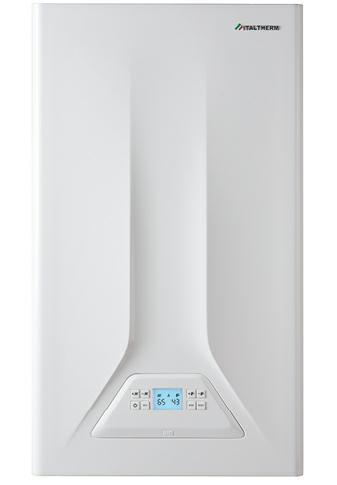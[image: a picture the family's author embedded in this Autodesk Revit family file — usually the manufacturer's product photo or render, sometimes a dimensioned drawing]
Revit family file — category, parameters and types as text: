
# Revit family: City Top H K
name_source: partatom
category: Attrezzatura meccanica
units: mm (PartAtom-declared; Revit-internal decimal feet)

## family parameters
Classificazione = Nessuno
Condiviso = No
Host = Muro
Mantieni orientamento annotazione = No
Punto di calcolo locali = No
Quota connettore circolare = Usa diametro
Sempre verticale = Sì
Taglio con vuoti quando caricato = No
Tipo di parte = Normale

## types (2) — shared parameters
Depth = 324 mm  [stored 1.06299 ft]
Design country = Italy
Domestic Cold Water Diameter = 21 mm  [stored 0.0688976 ft]
Domestic Hot Water Diameter = 21 mm  [stored 0.0688976 ft]
Energetic efficiency (92/42/CEE) = n.d.
Flue outlet = 100 mm  [stored 0.328084 ft]
Gas Inlet Diameter = 26 mm
Height = 700 mm  [stored 2.29659 ft]
Hydronic Return Diameter = 26 mm
Hydronic Supply Diameter = 26 mm
IFC Classification = Boiler
Immagine tipo = city top.jpg
Manufacturer country = Italy
Manufacturer name = Italtherm S.p.A.
Material main = Metal
Material secondary = Plastic
Minimum heat output 50/30°C = 2 W
Minimum heat output 80/60°C = 2 W
NBS reference Description = Boilers
Omniclass Description = Condensing boilers
Power supply | Frequency (Hz) = 50 Hz
Power supply | Phase = 1
Power supply | Voltage (V) = 230 V
Product family = Heating
Product group = Thermal unit
Siphon with condensate drain = 25 mm  [stored 0.082021 ft]
Uniclass 2015 Name = Boilers
Width = 400 mm  [stored 1.31234 ft]
zero-valued in all types: Edition number, Prospetto di default

## per-type parameters (varying)
| type | Date of publishing | Efficiency 30% | Maximum heat output 50/30°C | Maximum heat output 80/60°C | Maximum heating heat input | Nominal efficiency 50/30°C | Nominal efficiency 80/60°C | Power consumption (W) | URL | URL ENG | Weight |
| City Top H 25 K | 12/09/2019 | 105.30% | 27 W | 24 W | 25 W | 104.40% | 96.20% | 86 W | www.italtherm.it/g/caldaia-a-gas-da-interno/caldaia-a-condensazione/city-top-k/25-kw | en.italtherm.it/g/wall-hung-condensing-boilers/gas-boiler/city-top-k/25-kw | 37.20 kg |
| City Top H 35 K | 12/09/2023 | 105.60% | 35 W | 32 W | 33 W | 105.10% | 97.10% | 110 W | www.italtherm.it/g/caldaia-a-gas-da-interno/caldaia-a-condensazione/city-top-k/35-kw | en.italtherm.it/g/wall-hung-condensing-boilers/gas-boiler/city-top-k/35-kw | 37.00 kg |

note: [stored X ft] marks values corroborated as IEEE doubles in the binary element streams (Revit-internal decimal feet)
